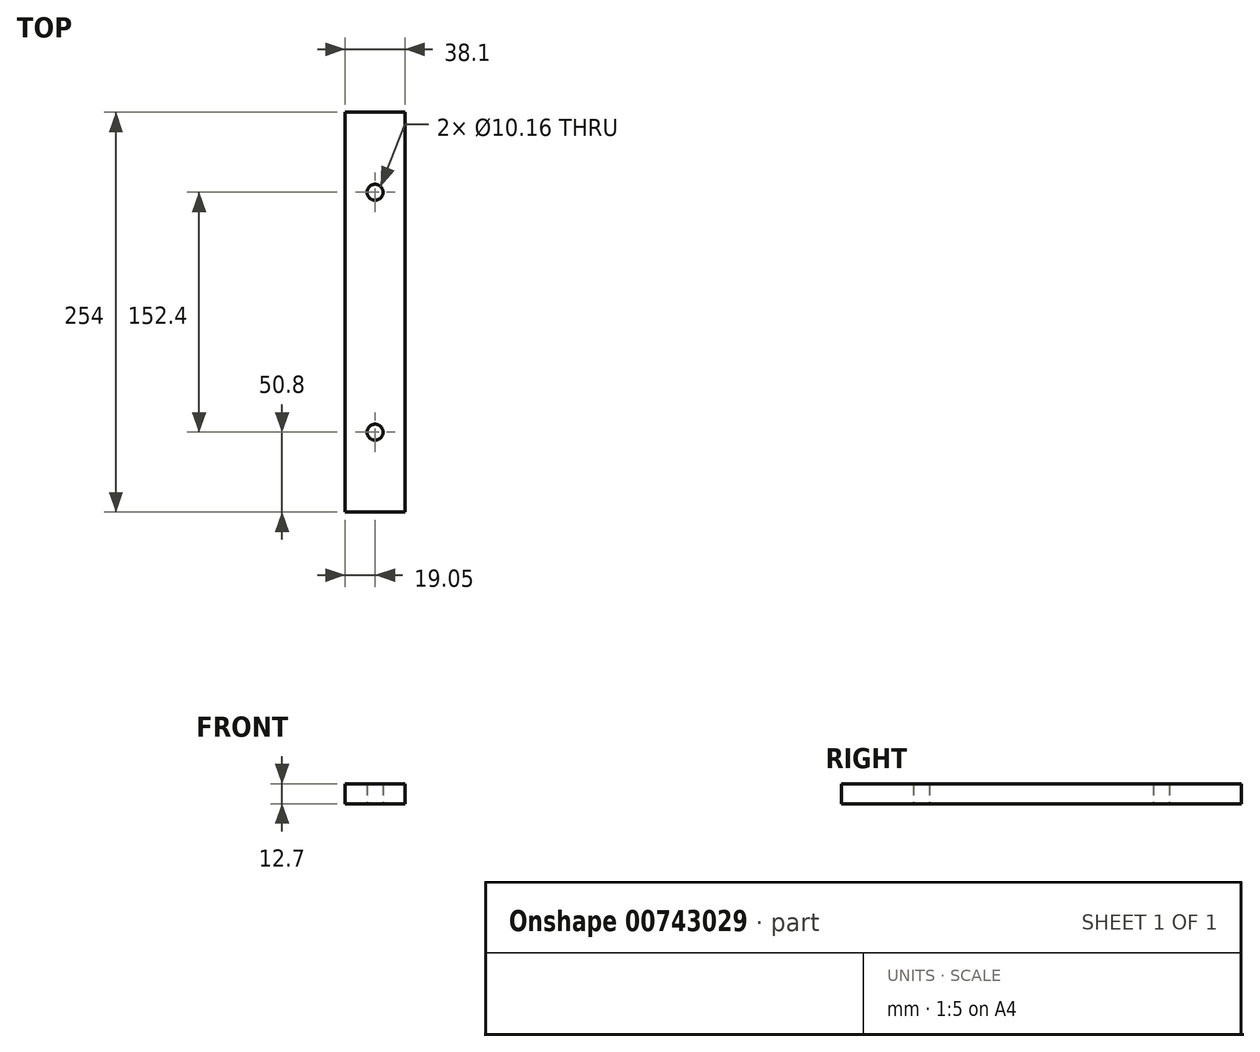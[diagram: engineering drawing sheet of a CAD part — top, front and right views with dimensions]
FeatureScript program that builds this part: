
annotation { "Feature Type Name" : "Feature", "Feature Type Description" : "" }
export const myFeature = defineFeature(function(context is Context, id is Id, definition is map)
    precondition{}
    {
        {
            var Q0;
            Q0=qCreatedBy(makeId("Top.planeOp"),FACE);
            var sketch = newSketch(context, id + "F0", { "sketchPlane" : qUnion([Q0])});
            skLineSegment(sketch, "E0.bottom", {"start": v(-19.05, -127) * mm, "end": v(19.05, -127) * mm});
            skLineSegment(sketch, "E0.top", {"start": v(-19.05, 127) * mm, "end": v(19.05, 127) * mm});
            skLineSegment(sketch, "E0.left", {"start": v(-19.05, -127) * mm, "end": v(-19.05, 127) * mm});
            skLineSegment(sketch, "E0.right", {"start": v(19.05, -127) * mm, "end": v(19.05, 127) * mm});
            skPoint(sketch, "E0.middle", {"position": v(0, 0) * mm});
            skSolve(sketch);
        }
        {
            var Q0;
            Q0=qSketchRegion(id+"F0",true);
            extrude(context, id + "F1", {"entities" : qUnion([Q0]), "oppositeDirection" : true, "depth" : 12.7 * mm, "offsetDistance" : 25.4 * mm});
        }
        {
            var Q0;
            Q0=makeQuery(id+"F0.imprint","IMPRINT",FACE,{"disambiguationData":[TD([[makeQuery(id+"F0.imprint","IMPRINT",EDGE,{"derivedFrom":sQuery(id+"F0.wireOp",EDGE,"E0.bottom")}),1.0]])]});
            var sketch = newSketch(context, id + "F2", { "sketchPlane" : qUnion([Q0])});
            skPoint(sketch, "E1", {"position": v(0, 76.2) * mm});
            skPoint(sketch, "E2", {"position": v(0, -76.2) * mm});
            skSolve(sketch);
        }
        {
            var Q0;
            Q0=sQuery(id+"F2.wireOp",VERTEX,"E1");
            var Q1;
            Q1=sQuery(id+"F2.wireOp",VERTEX,"E2");
            var Q2;
            Q2=makeQuery(id+"F1.opExtrude","SWEPT_BODY",BODY,{"disambiguationData":[OSD([sQuery(id+"F0.wireOp",EDGE,"E0.bottom"),sQuery(id+"F0.wireOp",EDGE,"E0.top"),sQuery(id+"F0.wireOp",EDGE,"E0.left"),sQuery(id+"F0.wireOp",EDGE,"E0.right")])]});
            hole(context, id + "F3", {"style" : HoleStyle.SIMPLE, "endStyle" : HoleEndStyle.THROUGH, "holeDiameter" : 10.16 * mm, "majorDiameter" : 6.35 * mm, "isTappedThrough" : true, "tappedDepth" : 12.7 * mm, "tapClearance" : 3, "locations" : qUnion([Q0, Q1]), "scope" : qUnion([Q2])});
        }
    });
